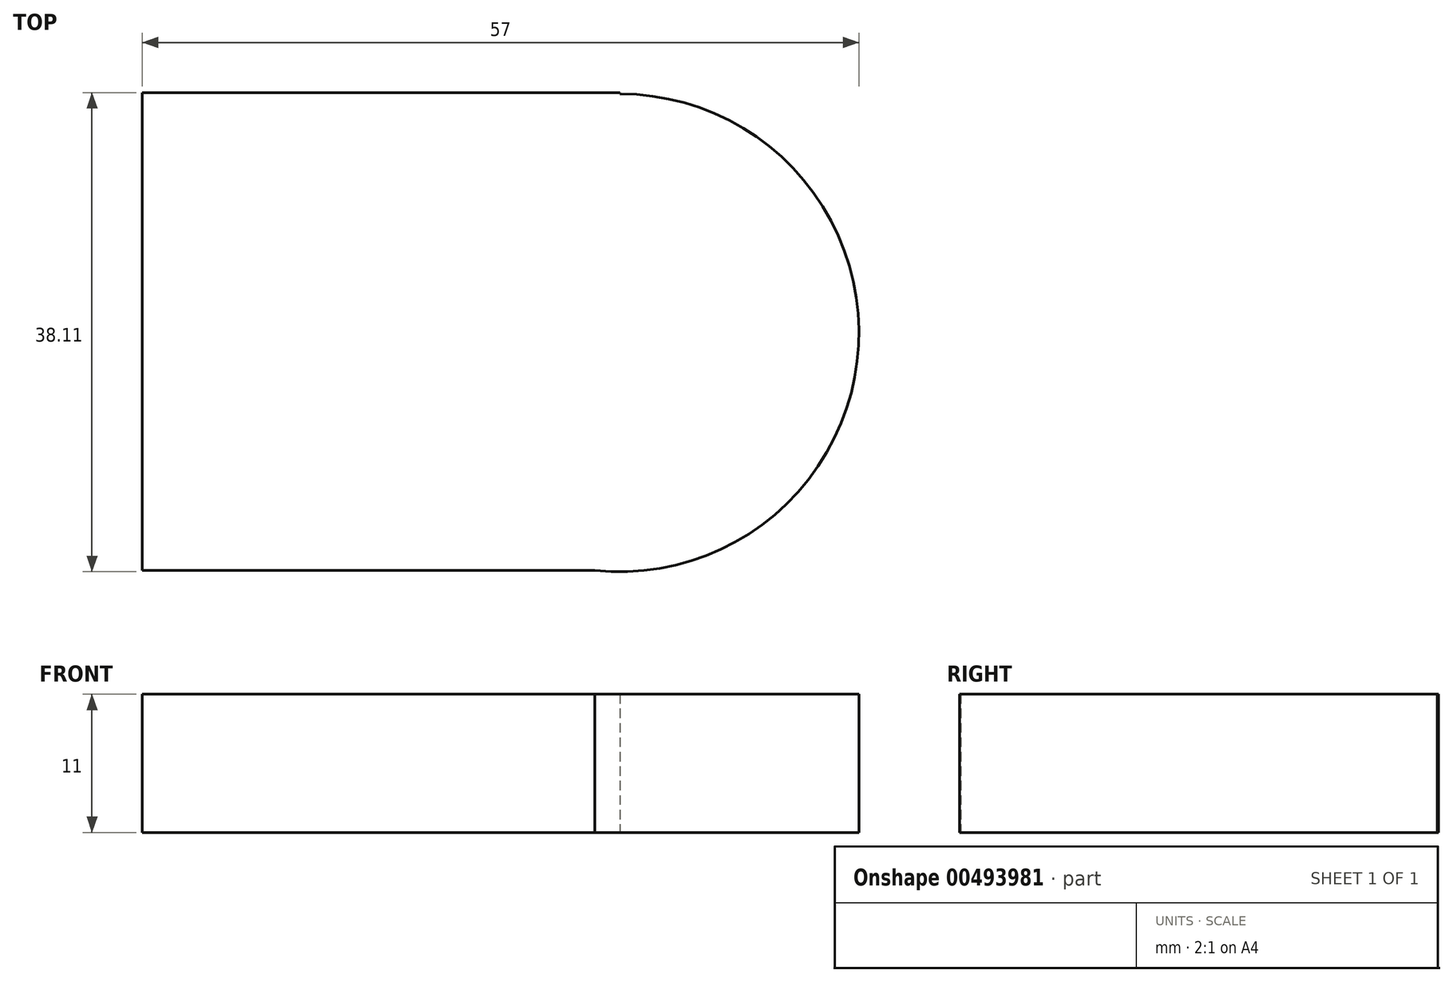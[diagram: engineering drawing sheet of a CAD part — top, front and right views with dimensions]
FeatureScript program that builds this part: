
annotation { "Feature Type Name" : "Feature", "Feature Type Description" : "" }
export const myFeature = defineFeature(function(context is Context, id is Id, definition is map)
    precondition{}
    {
        {
            var Q0;
            Q0=qCreatedBy(makeId("Top.planeOp"),FACE);
            var sketch = newSketch(context, id + "F0", { "sketchPlane" : qUnion([Q0])});
            skLineSegment(sketch, "E0.bottom", {"start": v(0, 0) * mm, "end": v(38, 0) * mm});
            skLineSegment(sketch, "E0.top", {"start": v(0, 38) * mm, "end": v(38, 38) * mm});
            skLineSegment(sketch, "E0.left", {"start": v(0, 0) * mm, "end": v(0, 38) * mm});
            skArc(sketch, "E1", {"start": v(36, 0) * mm, "mid": v(56.97, 17.89) * mm, "end": v(38, 37.9) * mm});
            skLineSegment(sketch, "E2.trimOffspring", {"start": v(38, 37.9) * mm, "end": v(38, 38) * mm});
            skSolve(sketch);
        }
        {
            var Q0;
            Q0 = qSketchRegion(id + "F0", true);
            extrude(context, id + "F1", {"entities" : qUnion([Q0]), "depth" : 11 * mm});
        }
    });
